# Revit family: Sink-Vessel-Lavatory-KALLISTA-Argile-P70368.rfa_
name_source: partatom
category: Plumbing Fixtures
units: mm (PartAtom-declared; Revit-internal decimal feet)

## family parameters
Cut with Voids When Loaded = No
Host = Face
OmniClass Number = 23.31.13.00
OmniClass Title = Sinks
Part Type = Normal
Room Calculation Point = No
Round Connector Dimension = Use Diameter
Shared = No

## types (2) — shared parameters
ADA Compliant = No
Assembly Code = D2010400
CW Connection = No
Cold Water Inlet = Cold Water Inlet
Date Modified = 02/06/2024
Default Elevation = 36"
Description = Edge Vessel
Drain Included = No
HW Connection = No
Height = 5 7/8"
Hot Water Inlet = Hot Water Inlet
Length = 20"
Manufacturer = Kallista Co.
Master Format 2014 = 22 41 16
Master Format 2014 Name = Residential Lavatories and Sinks
Material = Cast Stone
Product Name = Argile
URL = https://www.kallista.com
Vent Connection = No
Waste Connection = Yes
Waste Water Outlet = Waste Water Outlet
WaterSense Certified = No
Width = 13"

## per-type parameters (varying)
| type | Finish | Model | Product Documentation Link | Product Page URL | Type |
| HB1-Honed Black | Kallista-Cast_Stone-HB1-Honed_Black | P70368-00-HB1 |  |  | 1 |
| HW1-Honed White | Kallista-Cast_Stone-HW1-Honed_White | P70368-00-HW1 | https://resources.kohler.com | https://www.kallista.com | 2 |

## geometry (parser evidence)
native form markers: Sweep x5
no freeform markers — native parametric forms only
